FCSTD DOCUMENT  (FreeCAD 1.0R39319 (Git))
Label: Week2Sketch2
License: All rights reserved
LicenseURL: https://en.wikipedia.org/wiki/All_rights_reserved
objects: Sketcher::SketchObject×1, Spreadsheet::Sheet×1
note: 2 computed .brp shape members not serialized (recipe doc carries the construction recipe); baked Part::Feature solids carry a one-line shape summary decoded from their .brp

FEATURE [Sketcher::SketchObject] Sketch
  ArcFitTolerance = 1e-06
  FullyConstrained = true
  MakeInternals = false
  expr: Constraints[6] = <<Unnamed1>>#<<Spreadsheet>>.length
  expr: Constraints[7] = <<Unnamed1>>#<<Spreadsheet>>.diameter
  sketch-geometry (4):
    g0: ArcOfCircle CenterX=-3.2e-15 CenterY=120 CenterZ=0 NormalX=0 NormalY=0 NormalZ=1 AngleXU=0 Radius=120 StartAngle=1e-16 EndAngle=3.14159
    g1: ArcOfCircle CenterX=0 CenterY=0 CenterZ=0 NormalX=0 NormalY=0 NormalZ=1 AngleXU=0 Radius=120 StartAngle=3.14159 EndAngle=6.28319
    g2: LineSegment StartX=120 StartY=120 StartZ=0 EndX=120 EndY=-2.84e-14 EndZ=0
    g3: LineSegment StartX=-120 StartY=120 StartZ=0 EndX=-120 EndY=1.42e-14 EndZ=0
  constraints (9):
    c: Tangent(g0,g2) = 1.5708
    c: Tangent(g0,g3) = -1.5708
    c: Tangent(g1,g2) = 1.5708
    c: Tangent(g1,g3) = -1.5708
    c: Equal(g0,g1)
    c: Vertical(g2)
    c: DistanceY(g3,g3) = 120
    c: Radius(g1) = 120
    c: Coincident(g1,g-1)
FEATURE [Spreadsheet::Sheet] Spreadsheet
